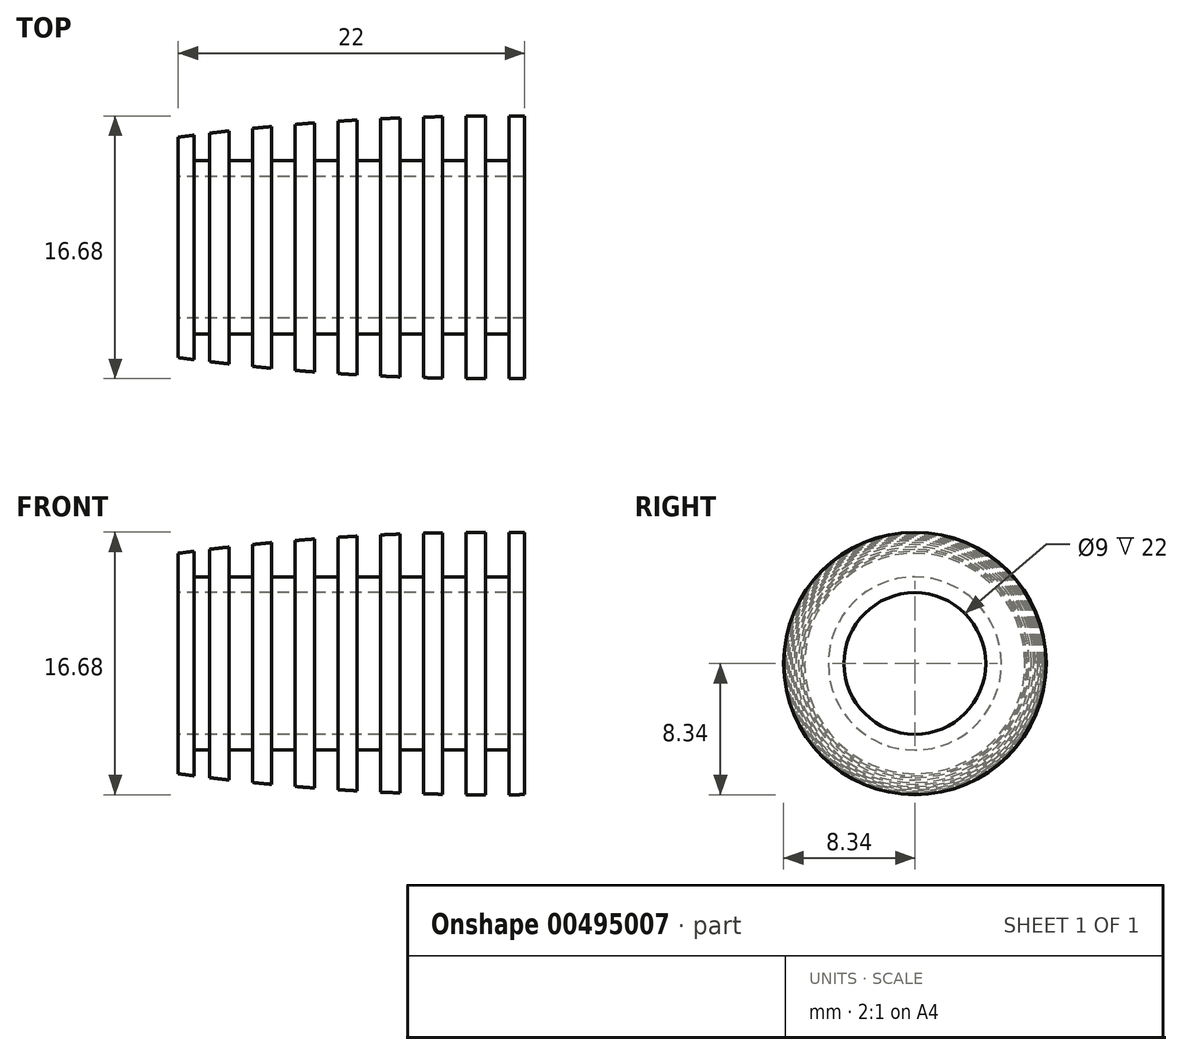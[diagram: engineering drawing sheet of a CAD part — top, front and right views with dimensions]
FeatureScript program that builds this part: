
annotation { "Feature Type Name" : "Feature", "Feature Type Description" : "" }
export const myFeature = defineFeature(function(context is Context, id is Id, definition is map)
    precondition{}
    {
        {
            var Q0;
            Q0=qCreatedBy(makeId("Front.planeOp"),FACE);
            var sketch = newSketch(context, id + "F0", { "sketchPlane" : qUnion([Q0])});
            skLineSegment(sketch, "E0.top", {"start": v(0, 4.5) * mm, "end": v(22, 4.5) * mm});
            skLineSegment(sketch, "E0.left", {"start": v(0, 7) * mm, "end": v(0, 4.5) * mm});
            skLineSegment(sketch, "E0.right", {"start": v(22, 8.33) * mm, "end": v(22, 4.5) * mm});
            skLineSegment(sketch, "E1", {"start": v(0, 0) * mm, "end": v(22, 0) * mm, "construction": true});
            skArc(sketch, "E2", {"start": v(22, 8.33) * mm, "mid": v(10.98, 8.07) * mm, "end": v(0, 7) * mm});
            skSolve(sketch);
        }
        {
            var Q0;
            Q0=makeQuery(id+"F0.imprint","IMPRINT",FACE,{"disambiguationData":[TD([[makeQuery(id+"F0.imprint","IMPRINT",EDGE,{"derivedFrom":sQuery(id+"F0.wireOp",EDGE,"E0.top")}),1.0]])]});
            var Q1;
            Q1=sQuery(id+"F0.wireOp",EDGE,"E1");
            revolve(context, id + "F1", {"entities" : qUnion([Q0]), "axis" : qUnion([Q1]), "revolveType" : RevolveType.FULL});
        }
        {
            var Q0;
            Q0=qCreatedBy(makeId("Front.planeOp"),FACE);
            var sketch = newSketch(context, id + "F2", { "sketchPlane" : qUnion([Q0])});
            skLineSegment(sketch, "E3.bottom", {"start": v(1, 9.5) * mm, "end": v(2, 9.5) * mm});
            skLineSegment(sketch, "E3.top", {"start": v(1, 5.5) * mm, "end": v(2, 5.5) * mm});
            skLineSegment(sketch, "E3.left", {"start": v(1, 9.5) * mm, "end": v(1, 5.5) * mm});
            skLineSegment(sketch, "E3.right", {"start": v(2, 9.5) * mm, "end": v(2, 5.5) * mm});
            skLineSegment(sketch, "E4.bottom", {"start": v(3.22, 5.5) * mm, "end": v(4.71, 5.5) * mm});
            skLineSegment(sketch, "E4.top", {"start": v(3.22, 9.5) * mm, "end": v(4.71, 9.5) * mm});
            skLineSegment(sketch, "E4.left", {"start": v(3.22, 5.5) * mm, "end": v(3.22, 9.5) * mm});
            skLineSegment(sketch, "E4.right", {"start": v(4.71, 5.5) * mm, "end": v(4.71, 9.5) * mm});
            skLineSegment(sketch, "E5.bottom", {"start": v(5.93, 5.5) * mm, "end": v(7.43, 5.5) * mm});
            skLineSegment(sketch, "E5.top", {"start": v(5.93, 9.5) * mm, "end": v(7.43, 9.5) * mm});
            skLineSegment(sketch, "E5.left", {"start": v(5.93, 5.5) * mm, "end": v(5.93, 9.5) * mm});
            skLineSegment(sketch, "E5.right", {"start": v(7.43, 5.5) * mm, "end": v(7.43, 9.5) * mm});
            skLineSegment(sketch, "E6.bottom", {"start": v(8.65, 5.5) * mm, "end": v(10.14, 5.5) * mm});
            skLineSegment(sketch, "E6.top", {"start": v(8.65, 9.5) * mm, "end": v(10.14, 9.5) * mm});
            skLineSegment(sketch, "E6.left", {"start": v(8.65, 5.5) * mm, "end": v(8.65, 9.5) * mm});
            skLineSegment(sketch, "E6.right", {"start": v(10.14, 5.5) * mm, "end": v(10.14, 9.5) * mm});
            skLineSegment(sketch, "E7.bottom", {"start": v(11.36, 5.5) * mm, "end": v(12.86, 5.5) * mm});
            skLineSegment(sketch, "E7.top", {"start": v(11.36, 9.5) * mm, "end": v(12.86, 9.5) * mm});
            skLineSegment(sketch, "E7.left", {"start": v(11.36, 5.5) * mm, "end": v(11.36, 9.5) * mm});
            skLineSegment(sketch, "E7.right", {"start": v(12.86, 5.5) * mm, "end": v(12.86, 9.5) * mm});
            skLineSegment(sketch, "E8.bottom", {"start": v(14.08, 5.5) * mm, "end": v(15.57, 5.5) * mm});
            skLineSegment(sketch, "E8.top", {"start": v(14.08, 9.5) * mm, "end": v(15.57, 9.5) * mm});
            skLineSegment(sketch, "E8.left", {"start": v(14.08, 5.5) * mm, "end": v(14.08, 9.5) * mm});
            skLineSegment(sketch, "E8.right", {"start": v(15.57, 5.5) * mm, "end": v(15.57, 9.5) * mm});
            skLineSegment(sketch, "E9.bottom", {"start": v(16.79, 5.5) * mm, "end": v(18.29, 5.5) * mm});
            skLineSegment(sketch, "E9.top", {"start": v(16.79, 9.5) * mm, "end": v(18.29, 9.5) * mm});
            skLineSegment(sketch, "E9.left", {"start": v(16.79, 5.5) * mm, "end": v(16.79, 9.5) * mm});
            skLineSegment(sketch, "E9.right", {"start": v(18.29, 5.5) * mm, "end": v(18.29, 9.5) * mm});
            skLineSegment(sketch, "E10.bottom", {"start": v(19.5, 5.5) * mm, "end": v(21, 5.5) * mm});
            skLineSegment(sketch, "E10.top", {"start": v(19.5, 9.5) * mm, "end": v(21, 9.5) * mm});
            skLineSegment(sketch, "E10.left", {"start": v(19.5, 5.5) * mm, "end": v(19.5, 9.5) * mm});
            skLineSegment(sketch, "E10.right", {"start": v(21, 5.5) * mm, "end": v(21, 9.5) * mm});
            skLineSegment(sketch, "E11", {"start": v(2, 9.5) * mm, "end": v(3.22, 9.5) * mm, "construction": true});
            skLineSegment(sketch, "E12", {"start": v(4.71, 9.5) * mm, "end": v(5.93, 9.5) * mm, "construction": true});
            skLineSegment(sketch, "E13", {"start": v(7.43, 9.5) * mm, "end": v(8.65, 9.5) * mm, "construction": true});
            skLineSegment(sketch, "E14", {"start": v(10.14, 9.5) * mm, "end": v(11.36, 9.5) * mm, "construction": true});
            skLineSegment(sketch, "E15", {"start": v(12.86, 9.5) * mm, "end": v(14.08, 9.5) * mm, "construction": true});
            skLineSegment(sketch, "E16", {"start": v(15.57, 9.5) * mm, "end": v(16.79, 9.5) * mm, "construction": true});
            skLineSegment(sketch, "E17", {"start": v(18.29, 9.5) * mm, "end": v(19.5, 9.5) * mm, "construction": true});
            skSolve(sketch);
        }
        {
            var Q0;
            Q0=makeQuery(id+"F2.imprint","IMPRINT",FACE,{"disambiguationData":[TD([[makeQuery(id+"F2.imprint","IMPRINT",EDGE,{"derivedFrom":sQuery(id+"F2.wireOp",EDGE,"E3.bottom")}),-1.0]])]});
            var Q1;
            Q1=makeQuery(id+"F2.imprint","IMPRINT",FACE,{"disambiguationData":[TD([[makeQuery(id+"F2.imprint","IMPRINT",EDGE,{"derivedFrom":sQuery(id+"F2.wireOp",EDGE,"E4.bottom")}),1.0]])]});
            var Q2;
            Q2=makeQuery(id+"F2.imprint","IMPRINT",FACE,{"disambiguationData":[TD([[makeQuery(id+"F2.imprint","IMPRINT",EDGE,{"derivedFrom":sQuery(id+"F2.wireOp",EDGE,"E5.bottom")}),1.0]])]});
            var Q3;
            Q3=makeQuery(id+"F2.imprint","IMPRINT",FACE,{"disambiguationData":[TD([[makeQuery(id+"F2.imprint","IMPRINT",EDGE,{"derivedFrom":sQuery(id+"F2.wireOp",EDGE,"E6.bottom")}),1.0]])]});
            var Q4;
            Q4=makeQuery(id+"F2.imprint","IMPRINT",FACE,{"disambiguationData":[TD([[makeQuery(id+"F2.imprint","IMPRINT",EDGE,{"derivedFrom":sQuery(id+"F2.wireOp",EDGE,"E7.bottom")}),1.0]])]});
            var Q5;
            Q5=makeQuery(id+"F2.imprint","IMPRINT",FACE,{"disambiguationData":[TD([[makeQuery(id+"F2.imprint","IMPRINT",EDGE,{"derivedFrom":sQuery(id+"F2.wireOp",EDGE,"E8.bottom")}),1.0]])]});
            var Q6;
            Q6=makeQuery(id+"F2.imprint","IMPRINT",FACE,{"disambiguationData":[TD([[makeQuery(id+"F2.imprint","IMPRINT",EDGE,{"derivedFrom":sQuery(id+"F2.wireOp",EDGE,"E9.bottom")}),1.0]])]});
            var Q7;
            Q7=makeQuery(id+"F2.imprint","IMPRINT",FACE,{"disambiguationData":[TD([[makeQuery(id+"F2.imprint","IMPRINT",EDGE,{"derivedFrom":sQuery(id+"F2.wireOp",EDGE,"E10.bottom")}),1.0]])]});
            var Q8;
            Q8=makeQuery(id+"F1.opRevolve","SWEPT_FACE",FACE,{"disambiguationData":[OSD([sQuery(id+"F0.wireOp",EDGE,"E0.top")])]});
            revolve(context, id + "F3", {"operationType" : NewBodyOperationType.REMOVE, "entities" : qUnion([Q0, Q1, Q2, Q3, Q4, Q5, Q6, Q7]), "axis" : qUnion([Q8]), "revolveType" : RevolveType.FULL, "oppositeDirection" : true});
        }
    });
